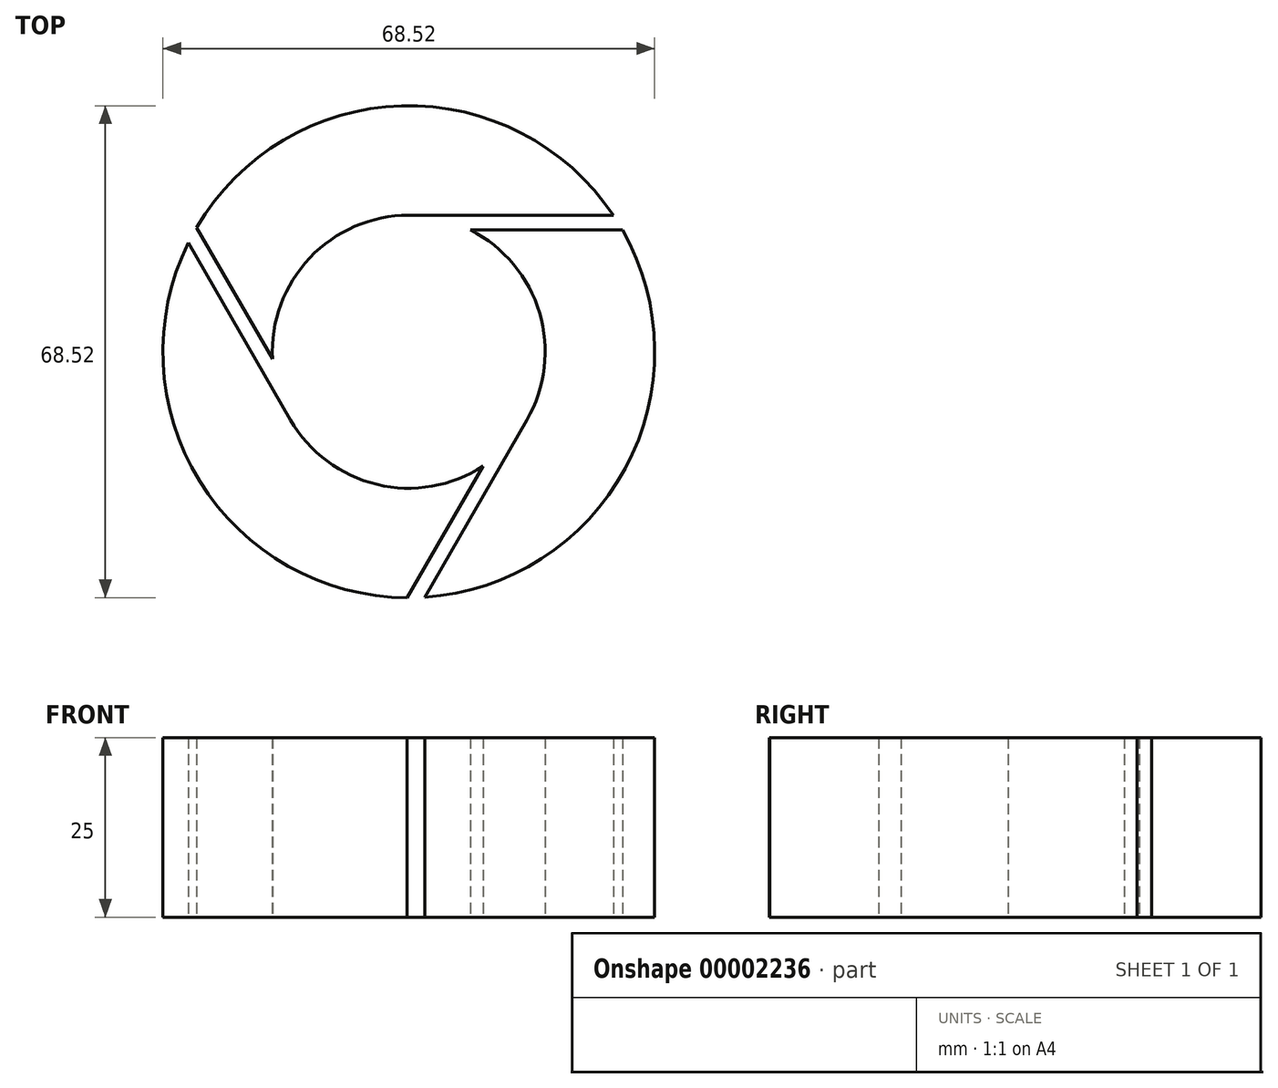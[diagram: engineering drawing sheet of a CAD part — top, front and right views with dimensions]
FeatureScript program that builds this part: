
annotation { "Feature Type Name" : "Feature", "Feature Type Description" : "" }
export const myFeature = defineFeature(function(context is Context, id is Id, definition is map)
    precondition{}
    {
        {
            var Q0;
            Q0=qCreatedBy(makeId("Top.planeOp"),FACE);
            var sketch = newSketch(context, id + "F0", { "sketchPlane" : qUnion([Q0])});
            skCircle(sketch, "E0", {"center": v(0, 0) * mm, "radius": 19.01 * mm, "construction": true});
            skCircle(sketch, "E1", {"center": v(0, 0) * mm, "radius": 34.26 * mm, "construction": true});
            skLineSegment(sketch, "E2", {"start": v(0, 19.01) * mm, "end": v(28.5, 19.01) * mm});
            skLineSegment(sketch, "E3", {"start": v(-15.61, -10.85) * mm, "end": v(-30.68, 15.25) * mm, "construction": true});
            skLineSegment(sketch, "E4.0", {"start": v(-13.88, -9.85) * mm, "end": v(-28.95, 16.25) * mm, "construction": true});
            skLineSegment(sketch, "E5", {"start": v(-18.98, -1) * mm, "end": v(-29.56, 17.32) * mm});
            skPoint(sketch, "E6", {"position": v(-8.15, 33.28) * mm});
            skArc(sketch, "E7", {"start": v(28.5, 19.01) * mm, "mid": v(-1, 34.25) * mm, "end": v(-29.56, 17.32) * mm});
            skPoint(sketch, "E8", {"position": v(-12.08, 14.68) * mm});
            skArc(sketch, "E9", {"start": v(0, 19.01) * mm, "mid": v(-13.8, 13.08) * mm, "end": v(-18.98, -1) * mm});
            skSolve(sketch);
        }
        {
            var Q0;
            Q0 = qSketchRegion(id + "F0", true);
            extrude(context, id + "F1", {"entities" : qUnion([Q0]), "depth" : 25 * mm});
        }
        {
            var Q0;
            Q0=qCreatedBy(makeId("Right.planeOp"),FACE);
            var sketch = newSketch(context, id + "F2", { "sketchPlane" : qUnion([Q0])});
            skLineSegment(sketch, "E10", {"start": v(0, 0) * mm, "end": v(0, 63.33) * mm});
            skSolve(sketch);
        }
        {
            var Q0;
            Q0=makeQuery(id+"F1.opExtrude","SWEPT_BODY",BODY,{"disambiguationData":[OSD([sQuery(id+"F0.wireOp",EDGE,"E2"),sQuery(id+"F0.wireOp",EDGE,"E5"),sQuery(id+"F0.wireOp",EDGE,"E7"),sQuery(id+"F0.wireOp",EDGE,"E9")])]});
            var Q1;
            Q1=sQuery(id+"F2.wireOp",EDGE,"E10");
            circularPattern(context, id + "F3", {"entities" : qUnion([Q0]), "axis" : qUnion([Q1]), "angle" : 120 * degree, "instanceCount" : 3});
        }
    });
